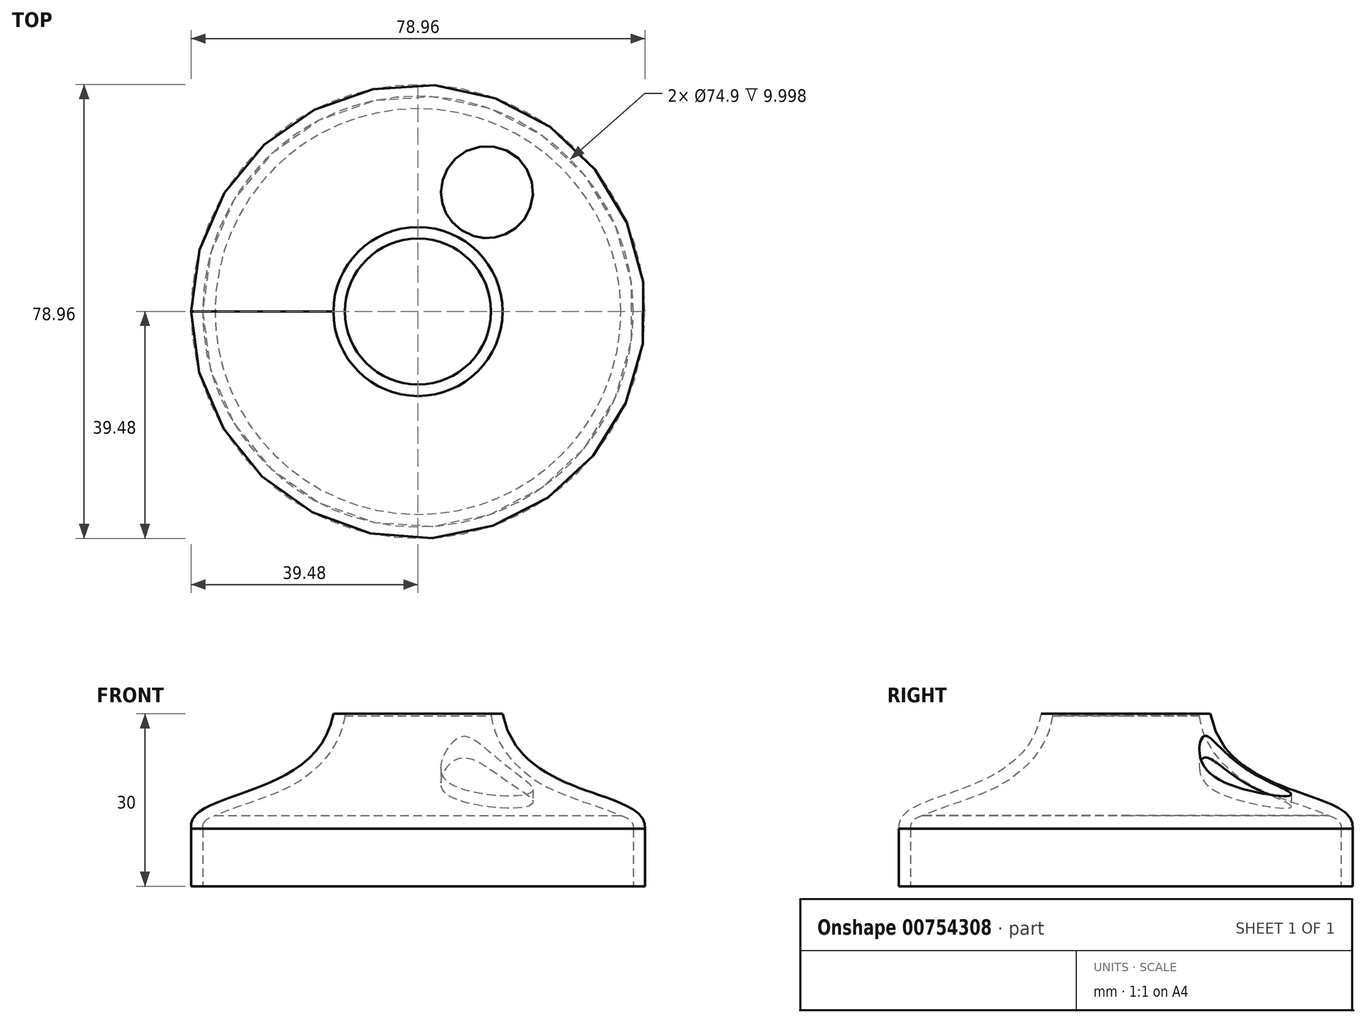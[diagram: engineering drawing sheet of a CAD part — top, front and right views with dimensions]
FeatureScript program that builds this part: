
annotation { "Feature Type Name" : "Feature", "Feature Type Description" : "" }
export const myFeature = defineFeature(function(context is Context, id is Id, definition is map)
    precondition{}
    {
        {
            var Q0;
            Q0=qCreatedBy(makeId("Front.planeOp"),FACE);
            var sketch = newSketch(context, id + "F0", { "sketchPlane" : qUnion([Q0])});
            skLineSegment(sketch, "E0", {"start": v(0, 0) * mm, "end": v(-36.25, 0) * mm, "construction": true});
            skLineSegment(sketch, "E1", {"start": v(-36.25, 0) * mm, "end": v(-37.45, 0) * mm, "construction": true});
            skLineSegment(sketch, "E2", {"start": v(-37.45, 0) * mm, "end": v(-37.45, -5) * mm});
            skLineSegment(sketch, "E3", {"start": v(-37.45, -5) * mm, "end": v(-39.45, -5) * mm});
            skLineSegment(sketch, "E4", {"start": v(-39.45, -5) * mm, "end": v(-39.45, 5) * mm});
            skLineSegment(sketch, "E5", {"start": v(0, 0) * mm, "end": v(0, 25) * mm, "construction": true});
            skLineSegment(sketch, "E6", {"start": v(0, 25) * mm, "end": v(-12.7, 25) * mm, "construction": true});
            skLineSegment(sketch, "E7", {"start": v(-12.7, 25) * mm, "end": v(-14.7, 25) * mm});
            skFitSpline(sketch, "E8", {"points": [v(-14.7, 25) * mm, v(-39.45, 5) * mm], "startDerivative": vector(-8.46, -45.58) * mm, "endDerivative": vector(2.66, -21.1) * mm});
            skFitSpline(sketch, "E9.0", {"points": [v(-12.73, 24.63) * mm, v(-12.93, 23.56) * mm, v(-13.51, 21.55) * mm, v(-14.86, 18.93) * mm, v(-16.59, 16.7) * mm, v(-19.26, 14.23) * mm, v(-23.08, 11.93) * mm, v(-27.03, 10.32) * mm, v(-30.02, 9.25) * mm, v(-32.12, 8.52) * mm, v(-33.98, 7.84) * mm, v(-35.54, 7.16) * mm, v(-36.49, 6.61) * mm, v(-37, 6.21) * mm, v(-37.25, 5.95) * mm, v(-37.39, 5.75) * mm, v(-37.45, 5.6) * mm, v(-37.48, 5.48) * mm, v(-37.48, 5.34) * mm, v(-37.47, 5.25) * mm]});
            skLineSegment(sketch, "E10", {"start": v(-37.45, 0) * mm, "end": v(-37.45, 5) * mm});
            skFitSpline(sketch, "E11", {"points": [v(-37.45, 5) * mm, v(-35.13, 7.32) * mm], "startDerivative": vector(-0.1, 1.7) * mm, "endDerivative": vector(6.85, 1.83) * mm});
            skLineSegment(sketch, "E12", {"start": v(-12.7, 25) * mm, "end": v(-12.73, 24.63) * mm});
            skSolve(sketch);
        }
        {
            var Q0;
            Q0=makeQuery(id+"F0.imprint","IMPRINT",FACE,{"disambiguationData":[TD([[makeQuery(id+"F0.imprint","IMPRINT",EDGE,{"derivedFrom":sQuery(id+"F0.wireOp",EDGE,"E2")}),-1.0]])]});
            var Q1;
            Q1=sQuery(id+"F0.wireOp",EDGE,"E5");
            revolve(context, id + "F1", {"surfaceOperationType" : NewSurfaceOperationType.NEW, "entities" : qUnion([Q0]), "axis" : qUnion([Q1]), "revolveType" : RevolveType.FULL});
        }
        {
            var Q0;
            Q0=qCreatedBy(makeId("Top.planeOp"),FACE);
            var sketch = newSketch(context, id + "F2", { "sketchPlane" : qUnion([Q0])});
            skCircle(sketch, "E13", {"center": v(0, 0) * mm, "radius": 24 * mm, "construction": true});
            skLineSegment(sketch, "E14", {"start": v(0, 0) * mm, "end": v(26.65, 46.16) * mm, "construction": true});
            skCircle(sketch, "E15", {"center": v(12, 20.78) * mm, "radius": 8 * mm});
            skSolve(sketch);
        }
        {
            var Q0;
            Q0 = qSketchRegion(id + "F2", true);
            extrude(context, id + "F3", {"entities" : qUnion([Q0]), "operationType" : NewBodyOperationType.REMOVE, "depth" : 25 * mm, "offsetDistance" : 25 * mm, "hasSecondDirection" : true, "secondDirectionOppositeDirection" : true, "secondDirectionDepth" : 25 * mm});
        }
    });
